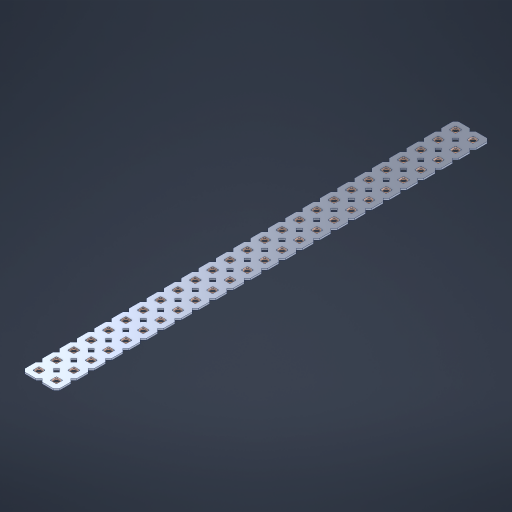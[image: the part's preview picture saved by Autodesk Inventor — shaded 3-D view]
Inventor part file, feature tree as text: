
AUTODESK INVENTOR PART (.ipt)
format: ipt  version: 2023 (Build 270158000, 158)  size: 839,680 bytes
history: native  units: in
note: dims shown in document units (in); Inventor stores cm internally (conversion verified against a paired STEP export)
features: other x51, extrude x49, sketch x2, pattern_linear x1
ambient origin geometry x8: Origin, YZ Plane, XZ Plane, XY Plane, X Axis, Y Axis, Z Axis, Center Point
bodies: Solid1 (feature_tree), Body (feature_tree)
feature tree (103):
  pattern_linear  "Rectangular Pattern1"  Spacing1=0.09in  [1 undecoded]
  sketch  "Sketch1"  dims[d1=0.5in]
  sketch  "Sketch2"  dims[d2=0.182in d3=0.09in d4=0.09in d5=0.09in d6=0.09in d7=0.09in d8=0.09in d9=0.09in d10=0.09in d11=0.02in d13=0.0in d14=0.172in d15=0.0625in d16=0.0in d19=0.5in d22=0.5in]
  other  "Srf1"
  other  "Srf126"
  other  "Srf127"
  other  "Srf128"
  other  "Srf129"
  other  "Srf130"
  other  "Srf131"
  other  "Srf250"
  other  "Srf251"
  other  "Srf252"
  other  "Srf253"
  other  "Srf254"
  other  "Srf255"
  other  "Srf256"
  other  "Srf257"
  other  "Srf258"
  other  "Srf259"
  other  "Srf260"
  other  "Srf261"
  other  "Srf262"
  other  "Srf263"
  other  "Srf264"
  other  "Srf265"
  other  "Srf266"
  other  "Srf267"
  other  "Srf268"
  other  "Srf269"
  other  "Srf270"
  other  "Srf271"
  other  "Srf272"
  other  "Srf273"
  other  "Srf274"
  other  "Srf275"
  other  "Srf276"
  other  "Srf277"
  other  "Srf278"
  other  "Srf279"
  other  "Srf280"
  other  "Srf281"
  other  "Srf282"
  other  "Srf283"
  other  "Srf284"
  other  "Srf285"
  other  "Srf286"
  other  "Srf287"
  other  "Srf288"
  other  "Srf289"
  other  "Srf290"
  other  "Srf291"
  other  "Srf292"
  other  "Circle"
  extrude  "ExtrusionSrf126"  Depth=0.09in
  extrude  "ExtrusionSrf127"  Depth=0.09in
  extrude  "ExtrusionSrf128"  Depth=0.09in
  extrude  "ExtrusionSrf129"  Depth=0.09in
  extrude  "ExtrusionSrf130"  Depth=0.09in
  extrude  "ExtrusionSrf131"  Depth=0.09in
  extrude  "ExtrusionSrf250"  Depth=0.09in
  extrude  "ExtrusionSrf251"  Depth=0.02in
  extrude  "ExtrusionSrf252"  TaperAngle=0.0deg  [1 undecoded]
  extrude  "ExtrusionSrf253"  Depth=0.5in
  extrude  "ExtrusionSrf254"  Depth=0.5in TaperAngle=0.0deg
  extrude  "ExtrusionSrf255"  Depth=0.5in
  extrude  "ExtrusionSrf256"  Depth=0.5in
  extrude  "ExtrusionSrf257"  [1 undecoded]
  extrude  "ExtrusionSrf258"  [1 undecoded]
  extrude  "ExtrusionSrf259"  [1 undecoded]
  extrude  "ExtrusionSrf260"  [1 undecoded]
  extrude  "ExtrusionSrf261"  [1 undecoded]
  extrude  "ExtrusionSrf262"  [1 undecoded]
  extrude  "ExtrusionSrf263"  [1 undecoded]
  extrude  "ExtrusionSrf264"  [1 undecoded]
  extrude  "ExtrusionSrf265"  [1 undecoded]
  extrude  "ExtrusionSrf266"  [1 undecoded]
  extrude  "ExtrusionSrf267"  [1 undecoded]
  extrude  "ExtrusionSrf268"  [1 undecoded]
  extrude  "ExtrusionSrf269"  [1 undecoded]
  extrude  "ExtrusionSrf270"  [1 undecoded]
  extrude  "ExtrusionSrf271"  [1 undecoded]
  extrude  "ExtrusionSrf272"  [1 undecoded]
  extrude  "ExtrusionSrf273"  [1 undecoded]
  extrude  "ExtrusionSrf274"  [1 undecoded]
  extrude  "ExtrusionSrf275"  [1 undecoded]
  extrude  "ExtrusionSrf276"  [1 undecoded]
  extrude  "ExtrusionSrf277"  [1 undecoded]
  extrude  "ExtrusionSrf278"  [1 undecoded]
  extrude  "ExtrusionSrf279"  [1 undecoded]
  extrude  "ExtrusionSrf280"  [1 undecoded]
  extrude  "ExtrusionSrf281"  [1 undecoded]
  extrude  "ExtrusionSrf282"  [1 undecoded]
  extrude  "ExtrusionSrf283"  [1 undecoded]
  extrude  "ExtrusionSrf284"  [1 undecoded]
  extrude  "ExtrusionSrf285"  [1 undecoded]
  extrude  "ExtrusionSrf286"  [1 undecoded]
  extrude  "ExtrusionSrf287"  [1 undecoded]
  extrude  "ExtrusionSrf288"  [1 undecoded]
  extrude  "ExtrusionSrf289"  [1 undecoded]
  extrude  "ExtrusionSrf290"  [1 undecoded]
  extrude  "ExtrusionSrf291"  [1 undecoded]
  extrude  "ExtrusionSrf292"  [1 undecoded]
note: 38 required parameter values undecoded (feature->parameter linkage not recoverable at this tier; creation-order binding heuristic only, values carry confidence <= 0.55)
